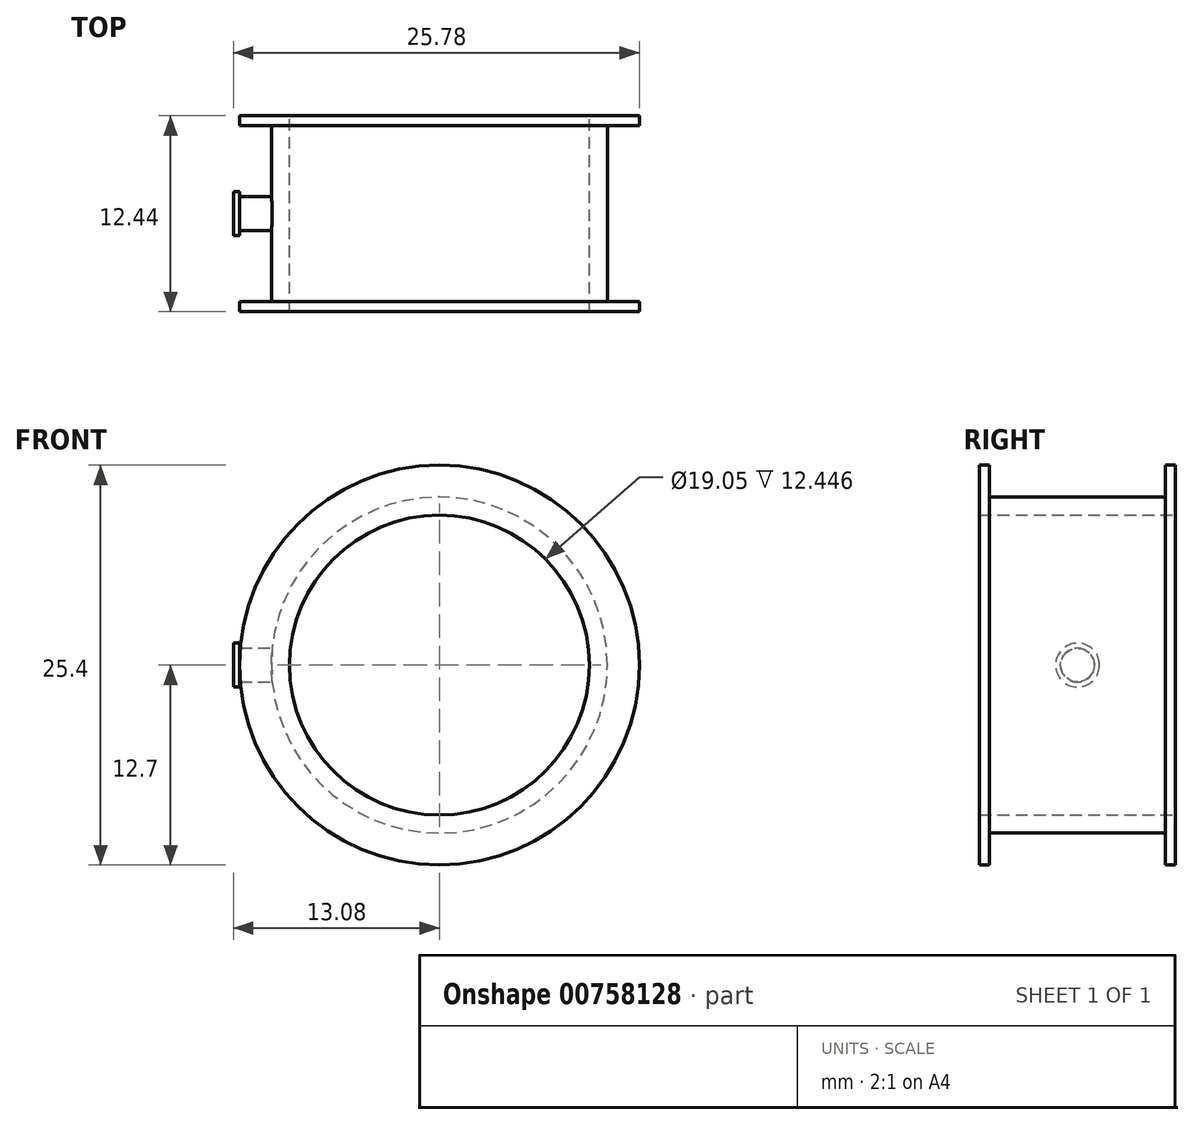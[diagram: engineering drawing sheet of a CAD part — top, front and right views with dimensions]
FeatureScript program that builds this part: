
annotation { "Feature Type Name" : "Feature", "Feature Type Description" : "" }
export const myFeature = defineFeature(function(context is Context, id is Id, definition is map)
    precondition{}
    {
        {
            var Q0;
            Q0=qCreatedBy(makeId("Front.planeOp"),FACE);
            var sketch = newSketch(context, id + "F0", { "sketchPlane" : qUnion([Q0])});
            skCircle(sketch, "E0", {"center": v(0, 0) * mm, "radius": 9.53 * mm});
            skCircle(sketch, "E1", {"center": v(0, 0) * mm, "radius": 12.7 * mm});
            skSolve(sketch);
        }
        {
            var Q0;
            Q0 = qSketchRegion(id + "F0", true);
            extrude(context, id + "F1", {"entities" : qUnion([Q0]), "endBound" : BoundingType.SYMMETRIC, "depth" : 12.45 * mm, "offsetDistance" : 25.4 * mm});
        }
        {
            var Q0;
            Q0=qCreatedBy(makeId("Front.planeOp"),FACE);
            var sketch = newSketch(context, id + "F2", { "sketchPlane" : qUnion([Q0])});
            skCircle(sketch, "E2", {"center": v(0, 0) * mm, "radius": 10.67 * mm});
            skCircle(sketch, "E3", {"center": v(0, 0) * mm, "radius": 15.24 * mm});
            skSolve(sketch);
        }
        {
            var Q0;
            Q0 = qSketchRegion(id + "F2", true);
            extrude(context, id + "F3", {"entities" : qUnion([Q0]), "operationType" : NewBodyOperationType.REMOVE, "endBound" : BoundingType.SYMMETRIC, "oppositeDirection" : true, "depth" : 11.18 * mm, "offsetDistance" : 25.4 * mm});
        }
        {
            var Q0;
            Q0=qCreatedBy(makeId("Right.planeOp"),FACE);
            var sketch = newSketch(context, id + "F4", { "sketchPlane" : qUnion([Q0])});
            skCircle(sketch, "E4", {"center": v(0, 0) * mm, "radius": 1.08 * mm});
            skSolve(sketch);
        }
        {
            var Q0;
            Q0=qCreatedBy(makeId("Top.planeOp"),FACE);
            var sketch = newSketch(context, id + "F5", { "sketchPlane" : qUnion([Q0])});
            skLineSegment(sketch, "E5", {"start": v(0, -23.09) * mm, "end": v(0, 28.73) * mm});
            skSolve(sketch);
        }
        {
            var Q0;
            Q0=makeQuery(id+"F4.imprint","IMPRINT",FACE,{"disambiguationData":[TD([[makeQuery(id+"F4.imprint","IMPRINT",EDGE,{"derivedFrom":sQuery(id+"F4.wireOp",EDGE,"E4")}),1.0]])]});
            extrude(context, id + "F6", {"entities" : qUnion([Q0]), "operationType" : NewBodyOperationType.ADD, "oppositeDirection" : true, "depth" : 12.7 * mm, "offsetDistance" : 25.4 * mm});
        }
        {
            var Q0;
            Q0=makeQuery(id+"F6.opExtrude","CAP_FACE",FACE,{"disambiguationData":[OSD([sQuery(id+"F4.wireOp",EDGE,"E4")])],"isStart":false});
            var sketch = newSketch(context, id + "F7", { "sketchPlane" : qUnion([Q0])});
            skCircle(sketch, "E6", {"center": v(0, 0) * mm, "radius": 1.4 * mm});
            skSolve(sketch);
        }
        {
            var Q0;
            Q0 = qSketchRegion(id + "F7", true);
            extrude(context, id + "F8", {"entities" : qUnion([Q0]), "operationType" : NewBodyOperationType.ADD, "depth" : 0.38 * mm, "offsetDistance" : 25.4 * mm});
        }
        {
            var Q0;
            Q0=makeQuery(id+"F1.opExtrude","CAP_FACE",FACE,{"disambiguationData":[OSD([sQuery(id+"F0.wireOp",EDGE,"E0"),sQuery(id+"F0.wireOp",EDGE,"E1")])],"isStart":false});
            var sketch = newSketch(context, id + "F9", { "sketchPlane" : qUnion([Q0])});
            skCircle(sketch, "E7", {"center": v(0, 0) * mm, "radius": 9.53 * mm});
            skSolve(sketch);
        }
        {
            var Q0;
            Q0 = qSketchRegion(id + "F9", true);
            extrude(context, id + "F10", {"entities" : qUnion([Q0]), "operationType" : NewBodyOperationType.REMOVE, "endBound" : BoundingType.THROUGH_ALL, "oppositeDirection" : true, "depth" : 25.4 * mm, "offsetDistance" : 25.4 * mm});
        }
    });
